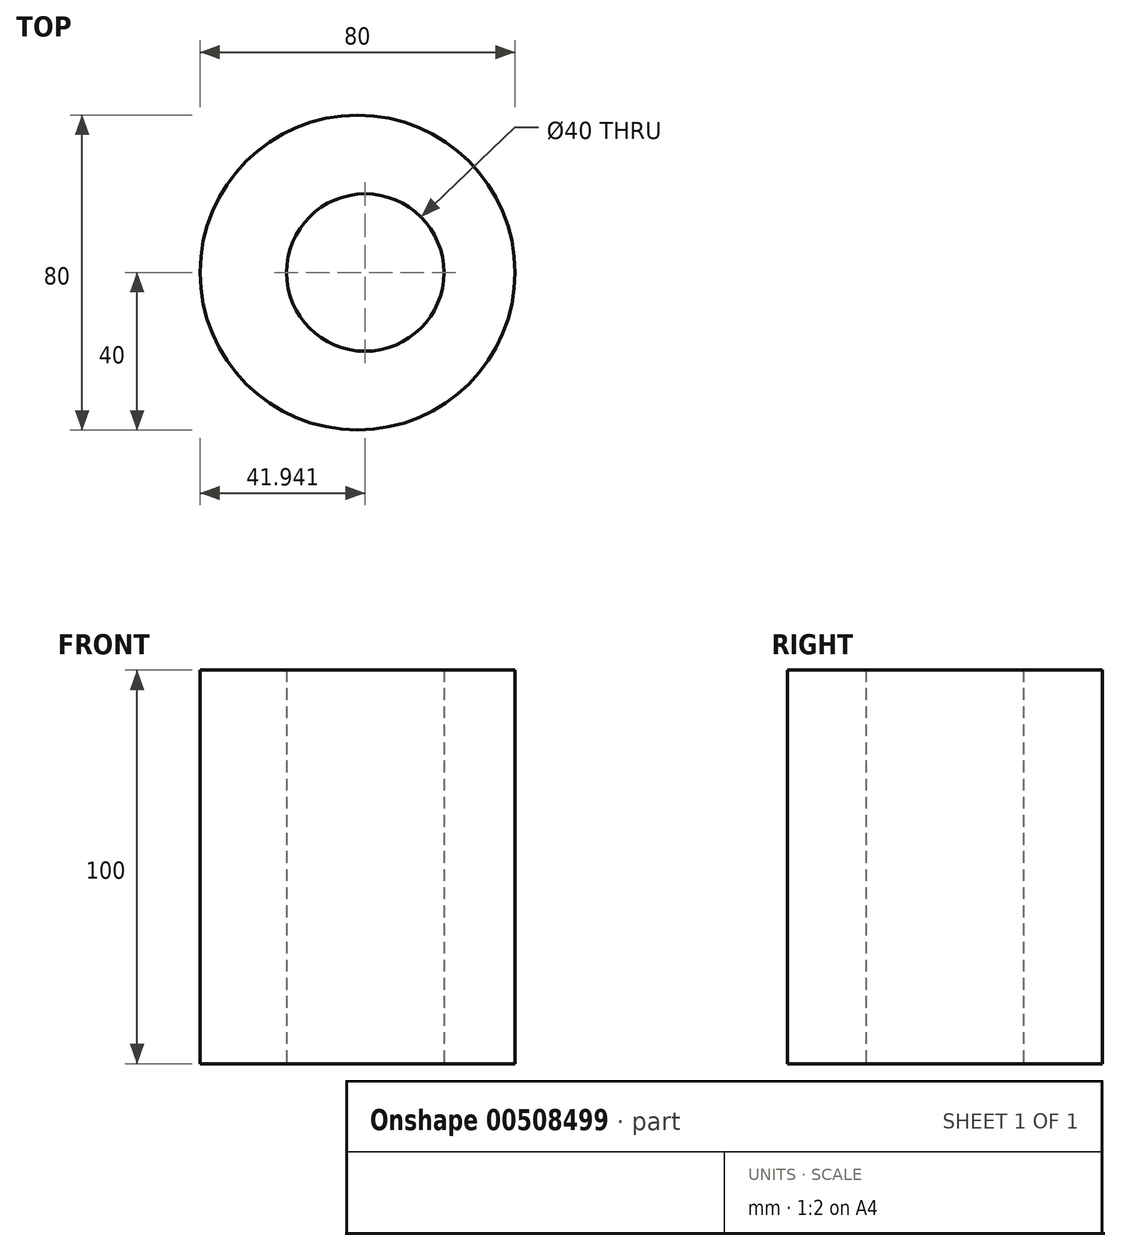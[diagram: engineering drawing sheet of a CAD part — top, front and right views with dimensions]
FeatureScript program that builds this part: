
annotation { "Feature Type Name" : "Feature", "Feature Type Description" : "" }
export const myFeature = defineFeature(function(context is Context, id is Id, definition is map)
    precondition{}
    {
        {
            var Q0;
            Q0=qCreatedBy(makeId("Top.planeOp"),FACE);
            var sketch = newSketch(context, id + "F0", { "sketchPlane" : qUnion([Q0])});
            skCircle(sketch, "E0", {"center": v(0, 0) * mm, "radius": 40 * mm});
            skCircle(sketch, "E1", {"center": v(1.94, 0) * mm, "radius": 20 * mm});
            skSolve(sketch);
        }
        {
            var Q0;
            Q0=makeQuery(id+"F0.imprint","IMPRINT",FACE,{"disambiguationData":[TD([[makeQuery(id+"F0.imprint","IMPRINT",EDGE,{"derivedFrom":sQuery(id+"F0.wireOp",EDGE,"E0")}),1.0]])]});
            extrude(context, id + "F1", {"entities" : qUnion([Q0]), "depth" : 100 * mm});
        }
    });
